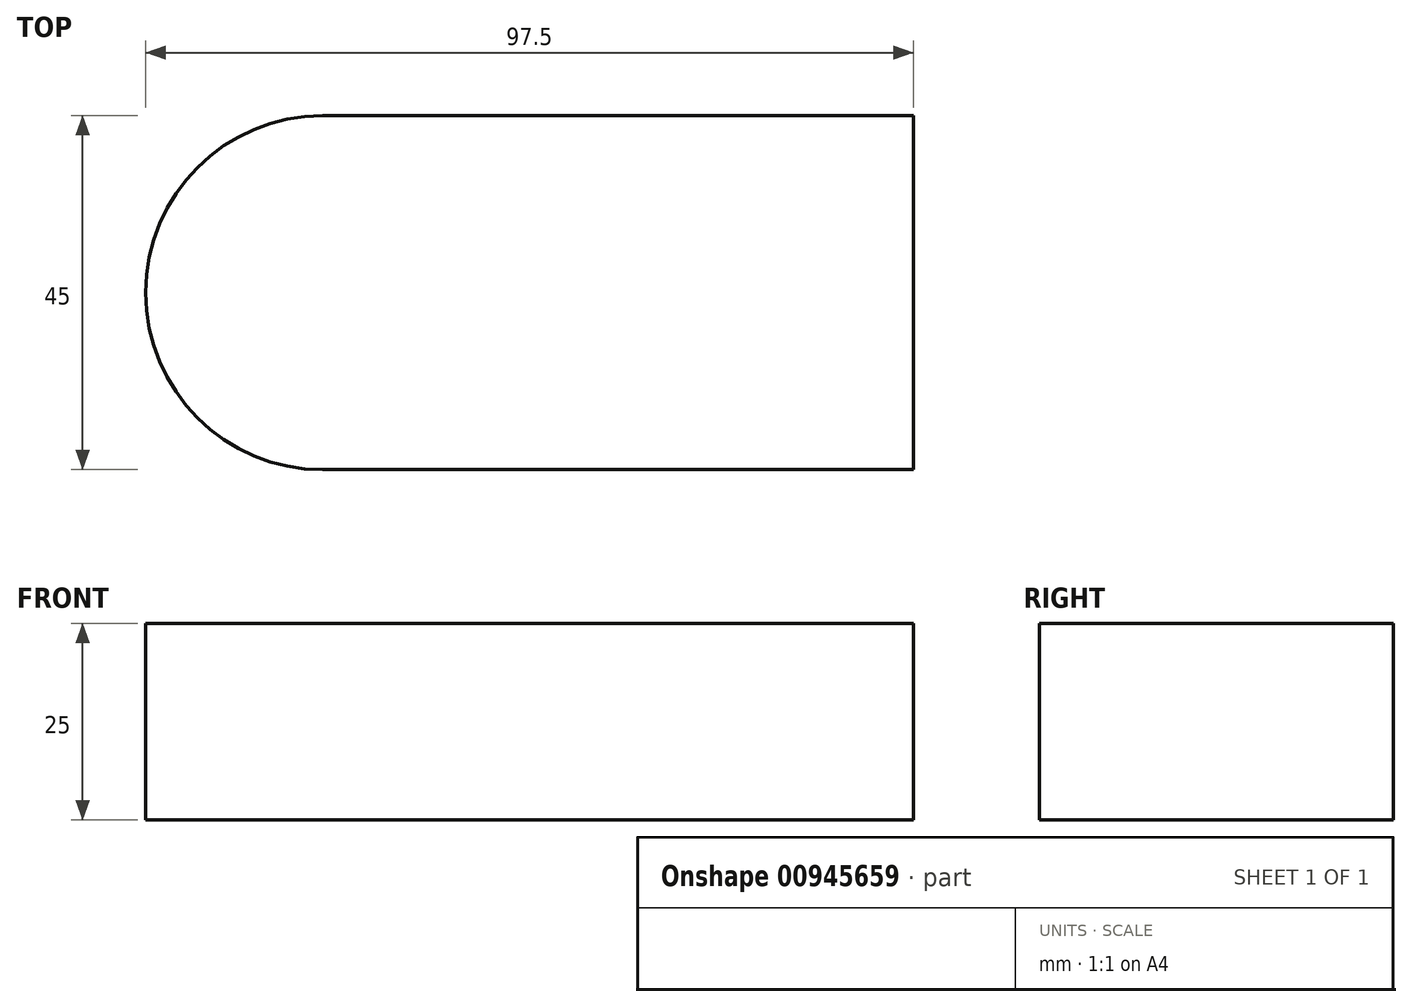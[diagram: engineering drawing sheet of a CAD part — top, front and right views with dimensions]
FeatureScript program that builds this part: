
annotation { "Feature Type Name" : "Feature", "Feature Type Description" : "" }
export const myFeature = defineFeature(function(context is Context, id is Id, definition is map)
    precondition{}
    {
        {
            var Q0;
            Q0=qCreatedBy(makeId("Top.planeOp"),FACE);
            var sketch = newSketch(context, id + "F0", { "sketchPlane" : qUnion([Q0])});
            skCircle(sketch, "E0", {"center": v(0, 0) * mm, "radius": 22.5 * mm});
            skLineSegment(sketch, "E1", {"start": v(0, 22.5) * mm, "end": v(75, 22.5) * mm});
            skLineSegment(sketch, "E2", {"start": v(75, 22.5) * mm, "end": v(75, -22.5) * mm});
            skLineSegment(sketch, "E3", {"start": v(75, -22.5) * mm, "end": v(0, -22.5) * mm});
            skSolve(sketch);
        }
        {
            var Q0;
            {var subQ0=sQuery(id+"F0.wireOp",EDGE,"E1");Q0=makeQuery(id+"F0.imprint","IMPRINT",FACE,{"disambiguationData":[TD([[makeQuery(id+"F0.imprint","IMPRINT",EDGE,{"derivedFrom":subQ0}),-1.0]])]});}
            var Q1;
            {var subQ0=sQuery(id+"F0.wireOp",EDGE,"E0");var subQ1=makeQuery(id+"F0.imprint","INTERSECT",VERTEX,{"derivedFrom":[subQ0,sQuery(id+"F0.wireOp",EDGE,"E1")]});Q1=makeQuery(id+"F0.imprint","IMPRINT",FACE,{"disambiguationData":[TD([[makeQuery(id+"F0.imprint","IMPRINT",EDGE,{"disambiguationData":[TD([[subQ1,-1.0]])],"derivedFrom":subQ0}),1.0]])]});}
            extrude(context, id + "F1", {"entities" : qUnion([Q0, Q1]), "depth" : 25 * mm, "offsetDistance" : 25 * mm});
        }
        {
            var Q0;
            {var subQ0=sQuery(id+"F0.wireOp",EDGE,"E0");var subQ1=makeQuery(id+"F0.imprint","INTERSECT",VERTEX,{"derivedFrom":[subQ0,sQuery(id+"F0.wireOp",EDGE,"E1")]});Q0=makeQuery(id+"F0.imprint","IMPRINT",FACE,{"disambiguationData":[TD([[makeQuery(id+"F0.imprint","IMPRINT",EDGE,{"disambiguationData":[TD([[subQ1,-1.0]])],"derivedFrom":subQ0}),1.0]])]});}
            extrude(context, id + "F2", {"entities" : qUnion([Q0]), "operationType" : NewBodyOperationType.ADD, "depth" : 25 * mm, "offsetDistance" : 25 * mm});
        }
    });
